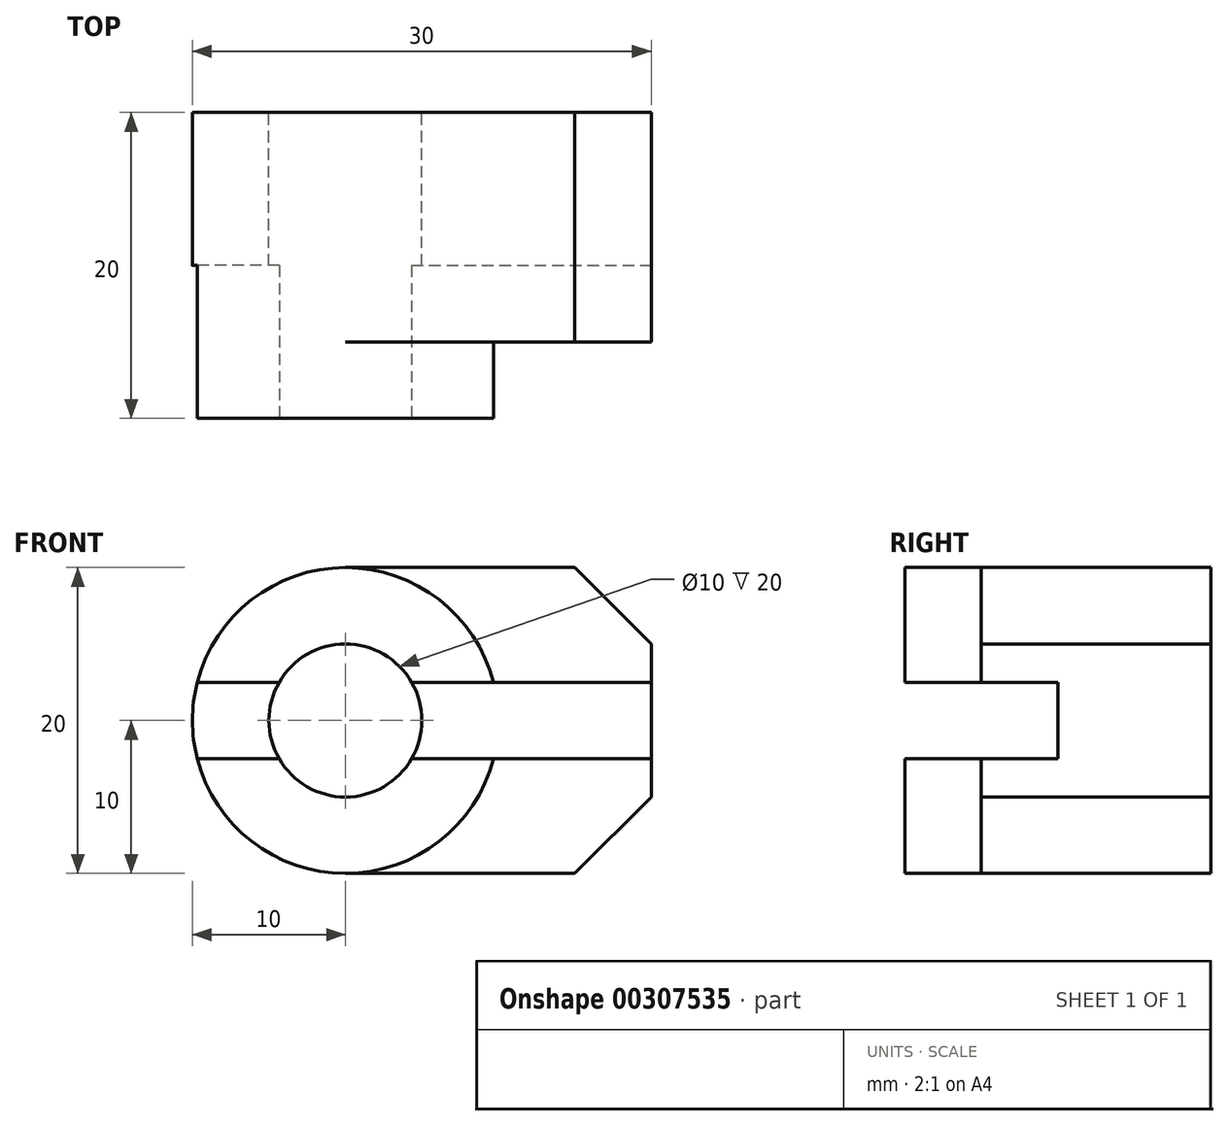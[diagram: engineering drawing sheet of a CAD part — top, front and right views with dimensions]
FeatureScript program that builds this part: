
annotation { "Feature Type Name" : "Feature", "Feature Type Description" : "" }
export const myFeature = defineFeature(function(context is Context, id is Id, definition is map)
    precondition{}
    {
        {
            var Q0;
            Q0=qCreatedBy(makeId("Front.planeOp"),FACE);
            var sketch = newSketch(context, id + "F0", { "sketchPlane" : qUnion([Q0])});
            skCircle(sketch, "E0", {"center": v(0, 0) * mm, "radius": 10 * mm});
            skCircle(sketch, "E1", {"center": v(0, 0) * mm, "radius": 5 * mm});
            skSolve(sketch);
        }
        {
            var Q0;
            Q0 = qSketchRegion(id + "F0", true);
            extrude(context, id + "F1", {"entities" : qUnion([Q0]), "depth" : 20 * mm});
        }
        {
            var Q0;
            Q0=qCreatedBy(makeId("Front.planeOp"),FACE);
            var sketch = newSketch(context, id + "F2", { "sketchPlane" : qUnion([Q0])});
            skArc(sketch, "E2", {"start": v(0, -10) * mm, "mid": v(10, 0) * mm, "end": v(0, 10) * mm});
            skLineSegment(sketch, "E3", {"start": v(0, 10) * mm, "end": v(15, 10) * mm});
            skLineSegment(sketch, "E4", {"start": v(20, 5) * mm, "end": v(20, -5) * mm});
            skLineSegment(sketch, "E5", {"start": v(0, -10) * mm, "end": v(15, -10) * mm});
            skLineSegment(sketch, "E6", {"start": v(15, -10) * mm, "end": v(20, -5) * mm});
            skLineSegment(sketch, "E7", {"start": v(15, 10) * mm, "end": v(20, 5) * mm});
            skPoint(sketch, "E8.orphan", {"position": v(20, -10) * mm});
            skPoint(sketch, "E9.orphan", {"position": v(20, 10) * mm});
            skSolve(sketch);
        }
        {
            var Q0;
            Q0 = qSketchRegion(id + "F2", true);
            extrude(context, id + "F3", {"entities" : qUnion([Q0]), "operationType" : NewBodyOperationType.ADD, "depth" : 15 * mm});
        }
        {
            var Q0;
            Q0=makeQuery(id+"F1.opExtrude","CAP_FACE",FACE,{"disambiguationData":[OSD([sQuery(id+"F0.wireOp",EDGE,"E0"),sQuery(id+"F0.wireOp",EDGE,"E1")])],"isStart":false});
            var sketch = newSketch(context, id + "F4", { "sketchPlane" : qUnion([Q0])});
            skLineSegment(sketch, "E10", {"start": v(4.33, -2.5) * mm, "end": v(20, -2.5) * mm});
            skLineSegment(sketch, "E11", {"start": v(4.33, 2.5) * mm, "end": v(20, 2.5) * mm});
            skLineSegment(sketch, "E12", {"start": v(20, 2.5) * mm, "end": v(20, -2.5) * mm});
            skArc(sketch, "E13", {"start": v(4.33, -2.5) * mm, "mid": v(5, 0) * mm, "end": v(4.33, 2.5) * mm});
            skLineSegment(sketch, "E14", {"start": v(-4.33, -2.5) * mm, "end": v(-9.68, -2.5) * mm});
            skLineSegment(sketch, "E15", {"start": v(-4.33, 2.5) * mm, "end": v(-9.68, 2.5) * mm});
            skArc(sketch, "E16", {"start": v(-9.68, 2.5) * mm, "mid": v(-10, 0) * mm, "end": v(-9.68, -2.5) * mm});
            skArc(sketch, "E17", {"start": v(-4.33, 2.5) * mm, "mid": v(-5, 0) * mm, "end": v(-4.33, -2.5) * mm});
            skSolve(sketch);
        }
        {
            var Q0;
            Q0 = qSketchRegion(id + "F4", true);
            extrude(context, id + "F5", {"entities" : qUnion([Q0]), "operationType" : NewBodyOperationType.REMOVE, "oppositeDirection" : true, "depth" : 10 * mm});
        }
    });
